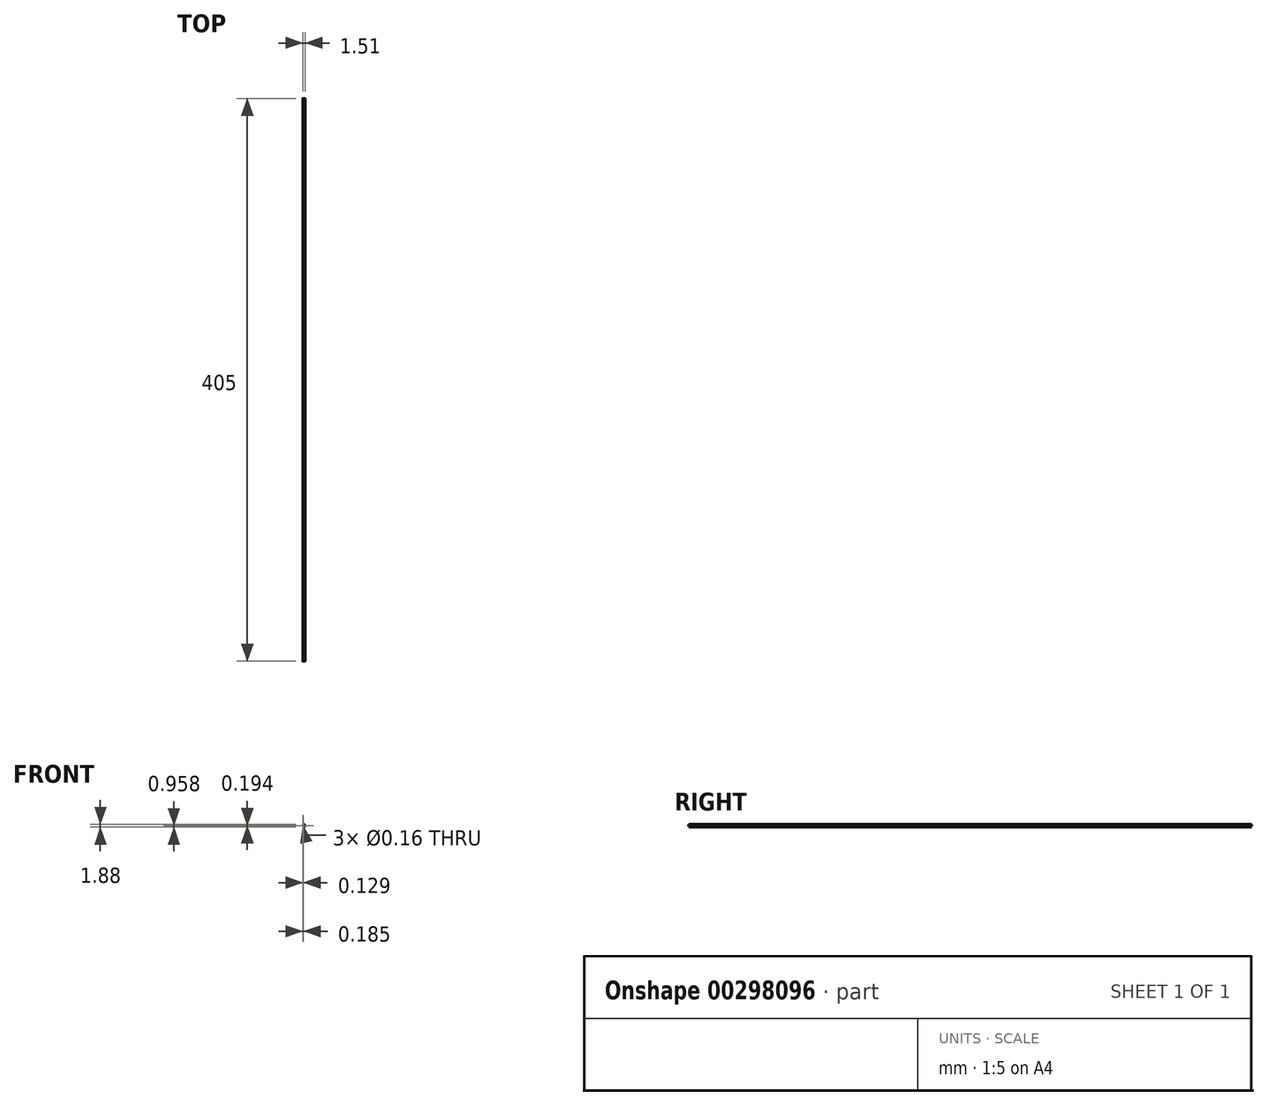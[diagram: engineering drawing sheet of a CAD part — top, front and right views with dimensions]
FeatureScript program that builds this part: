
annotation { "Feature Type Name" : "Feature", "Feature Type Description" : "" }
export const myFeature = defineFeature(function(context is Context, id is Id, definition is map)
    precondition{}
    {
        {
            var Q0;
            Q0=qCreatedBy(makeId("Front.planeOp"),FACE);
            var sketch = newSketch(context, id + "F0", { "sketchPlane" : qUnion([Q0])});
            skCircle(sketch, "E0", {"center": v(0, 0) * mm, "radius": 0.4 * mm});
            skCircle(sketch, "E1", {"center": v(-0.1, -0.56) * mm, "radius": 0.08 * mm});
            skCircle(sketch, "E2", {"center": v(0.1, -0.56) * mm, "radius": 0.08 * mm});
            skCircle(sketch, "E3", {"center": v(0, 0.84) * mm, "radius": 0.4 * mm});
            skCircle(sketch, "E4", {"center": v(0.65, 0.51) * mm, "radius": 0.08 * mm});
            skCircle(sketch, "E5", {"center": v(0.65, 0.32) * mm, "radius": 0.08 * mm});
            skCircle(sketch, "E6", {"center": v(0.47, 0.42) * mm, "radius": 0.08 * mm});
            skCircle(sketch, "E7", {"center": v(0.56, 0.42) * mm, "radius": 0.22 * mm});
            skEllipse(sketch, "E8", {"center": v(0, -0.56) * mm, "majorRadius": 0.23 * mm, "minorRadius": 0.11 * mm, "majorAxis": v(1, 0)});
            skCircle(sketch, "E9.MirrorC", {"center": v(-0.56, 0.42) * mm, "radius": 0.22 * mm});
            skCircle(sketch, "E10.MirrorC", {"center": v(-0.65, 0.51) * mm, "radius": 0.08 * mm});
            skCircle(sketch, "E11.MirrorC", {"center": v(-0.47, 0.42) * mm, "radius": 0.08 * mm});
            skCircle(sketch, "E12.MirrorC", {"center": v(-0.65, 0.32) * mm, "radius": 0.08 * mm});
            skPoint(sketch, "E13", {"position": v(0, 1.24) * mm});
            skPoint(sketch, "E14", {"position": v(0, -0.67) * mm});
            skPoint(sketch, "E15", {"position": v(0, 0.29) * mm});
            skCircle(sketch, "E16", {"center": v(0, 0.29) * mm, "radius": 1.2 * mm});
            skCircle(sketch, "E17", {"center": v(0, 0.29) * mm, "radius": 1.05 * mm});
            skSolve(sketch);
        }
        {
            var Q0;
            Q0=makeQuery(id+"F0.imprint","IMPRINT",FACE,{"disambiguationData":[TD([[makeQuery(id+"F0.imprint","IMPRINT",EDGE,{"derivedFrom":sQuery(id+"F0.wireOp",EDGE,"E3")}),1.0]])]});
            var Q1;
            Q1=makeQuery(id+"F0.imprint","IMPRINT",FACE,{"disambiguationData":[TD([[makeQuery(id+"F0.imprint","IMPRINT",EDGE,{"derivedFrom":sQuery(id+"F0.wireOp",EDGE,"E0")}),1.0]])]});
            var Q2;
            Q2=makeQuery(id+"F0.imprint","IMPRINT",FACE,{"disambiguationData":[TD([[makeQuery(id+"F0.imprint","IMPRINT",EDGE,{"derivedFrom":sQuery(id+"F0.wireOp",EDGE,"E11.MirrorC")}),-1.0]])]});
            var Q3;
            Q3=makeQuery(id+"F0.imprint","IMPRINT",FACE,{"disambiguationData":[TD([[makeQuery(id+"F0.imprint","IMPRINT",EDGE,{"derivedFrom":sQuery(id+"F0.wireOp",EDGE,"E10.MirrorC")}),-1.0]])]});
            var Q4;
            Q4=makeQuery(id+"F0.imprint","IMPRINT",FACE,{"disambiguationData":[TD([[makeQuery(id+"F0.imprint","IMPRINT",EDGE,{"derivedFrom":sQuery(id+"F0.wireOp",EDGE,"E12.MirrorC")}),-1.0]])]});
            var Q5;
            Q5=makeQuery(id+"F0.imprint","IMPRINT",FACE,{"disambiguationData":[TD([[makeQuery(id+"F0.imprint","IMPRINT",EDGE,{"derivedFrom":sQuery(id+"F0.wireOp",EDGE,"E6")}),1.0]])]});
            var Q6;
            Q6=makeQuery(id+"F0.imprint","IMPRINT",FACE,{"disambiguationData":[TD([[makeQuery(id+"F0.imprint","IMPRINT",EDGE,{"derivedFrom":sQuery(id+"F0.wireOp",EDGE,"E4")}),1.0]])]});
            var Q7;
            Q7=makeQuery(id+"F0.imprint","IMPRINT",FACE,{"disambiguationData":[TD([[makeQuery(id+"F0.imprint","IMPRINT",EDGE,{"derivedFrom":sQuery(id+"F0.wireOp",EDGE,"E5")}),1.0]])]});
            var Q8;
            Q8=makeQuery(id+"F0.imprint","IMPRINT",FACE,{"disambiguationData":[TD([[makeQuery(id+"F0.imprint","IMPRINT",EDGE,{"derivedFrom":sQuery(id+"F0.wireOp",EDGE,"E2")}),1.0]])]});
            var Q9;
            Q9=makeQuery(id+"F0.imprint","IMPRINT",FACE,{"disambiguationData":[TD([[makeQuery(id+"F0.imprint","IMPRINT",EDGE,{"derivedFrom":sQuery(id+"F0.wireOp",EDGE,"E1")}),1.0]])]});
            extrude(context, id + "F1", {"entities" : qUnion([Q0, Q1, Q2, Q3, Q4, Q5, Q6, Q7, Q8, Q9]), "depth" : 405 * mm});
        }
    });
